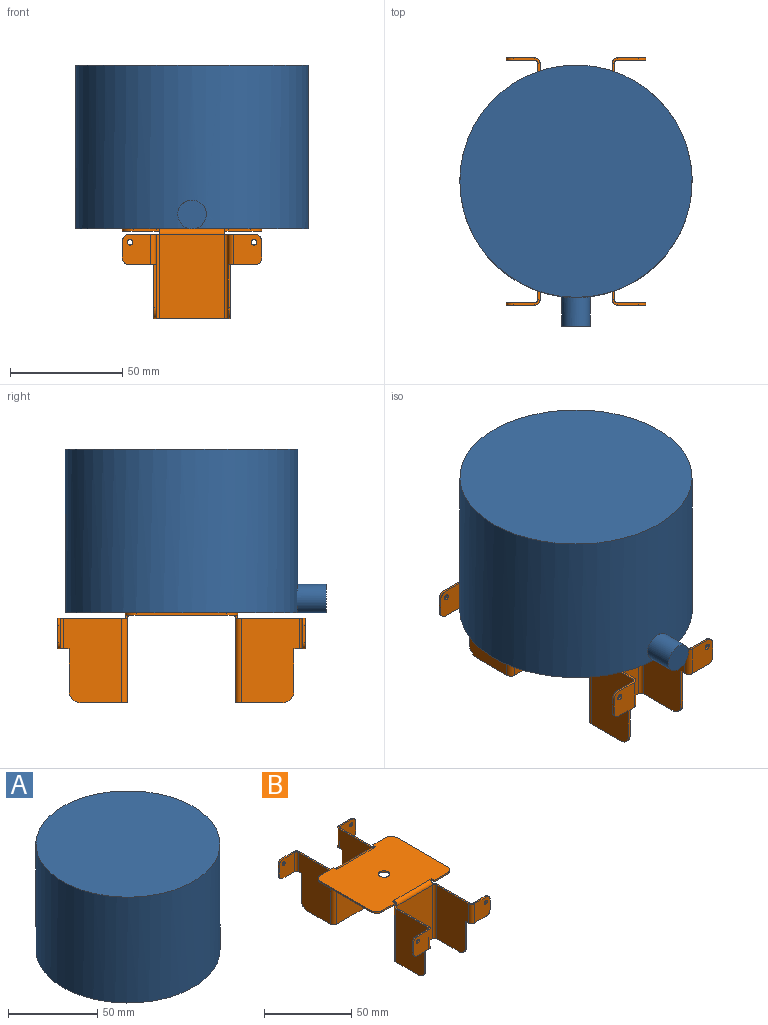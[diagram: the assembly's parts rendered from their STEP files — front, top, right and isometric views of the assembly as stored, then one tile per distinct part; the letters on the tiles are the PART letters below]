
ASSEMBLY  parts=2 mates=1
PART A: 5 faces, bbox 103.3x116x72.7 mm
  f0: cylinder r=51.65mm len=103.3mm, axis (0,0,-1), area 23466.2mm2, adj f1,f2,f4
  f1: plane 103.3x103.3mm, normal (0,0,1), area 8380.9mm2, adj f0
  f2: plane 103.3x103.3mm, normal (0,0,-1), area 8380.9mm2, adj f0
  f3: plane 12.7x12.7mm, normal (0,1,0), area 126.7mm2, adj f4
  f4: cylinder r=6.35mm len=13.09mm, axis (0,-1,0), area 514.5mm2, adj f0,f3
PART B: 127 faces, bbox 62x110x40 mm
  f0: plane 1.5x1mm, normal (0,-1,0), area 1.5mm2, adj f3,f15,f16,f123
  f1: plane 1.5x1mm, normal (0,1,0), area 1.5mm2, adj f5,f15,f16,f71
  f2: plane 2.5x1mm, normal (-1,0,0), area 2.5mm2, adj f10,f11,f15,f16
  f3: plane 2.5x1mm, normal (1,0,0), area 2.5mm2, adj f0,f9,f15,f16
  f4: plane 2.5x1mm, normal (1,0,0), area 2.5mm2, adj f6,f7,f15,f16
  f5: plane 2.5x1mm, normal (-1,0,0), area 2.5mm2, adj f1,f14,f15,f16
  f6: plane 1.5x1mm, normal (0,1,0), area 1.5mm2, adj f4,f15,f16,f70
  f7: plane 10x1mm, normal (0,1,0), area 10mm2, adj f4,f15,f16,f18
  f8: plane 40x1mm, normal (-1,0,0), area 40mm2, adj f15,f16,f18,f20
  f9: plane 10x1mm, normal (0,-1,0), area 10mm2, adj f3,f15,f16,f20
  f10: plane 1.5x1mm, normal (0,-1,0), area 1.5mm2, adj f2,f15,f16,f124
  f11: plane 10x1mm, normal (0,-1,0), area 10mm2, adj f2,f15,f16,f19
  f12: plane 40x1mm, normal (1,0,0), area 40mm2, adj f15,f16,f17,f19
  f13: cylinder r=3.26mm len=6.53mm, axis (0,0,1), area 20.5mm2, adj f15,f16
  f14: plane 10x1mm, normal (0,1,0), area 10mm2, adj f5,f15,f16,f17
  f15: plane 62x50mm, normal (0,0,1), area 2885.1mm2, adj f0,f1,f2,f3,f4,f5,f6,f7
  f16: plane 62x50mm, normal (0,0,-1), area 2885.1mm2, adj f0,f1,f2,f3,f4,f5,f6,f7
  f17: cylinder r=5mm len=5mm, axis (0,0,1), area 7.9mm2, adj f12,f14,f15,f16
  f18: cylinder r=5mm len=5mm, axis (0,0,1), area 7.9mm2, adj f7,f8,f15,f16
  f19: cylinder r=5mm len=5mm, axis (0,0,-1), area 7.9mm2, adj f11,f12,f15,f16
  f20: cylinder r=5mm len=5mm, axis (0,0,-1), area 7.9mm2, adj f8,f9,f15,f16
  f21: plane 29x1mm, normal (0,0,-1), area 29mm2, adj f22,f23,f44,f67
  f22: plane 37.5x29mm, normal (0,1,0), area 1087.5mm2, adj f21,f46,f69,f72
  f23: plane 37.5x29mm, normal (0,-1,0), area 1087.5mm2, adj f21,f45,f68,f73
  f24: plane 19x1mm, normal (0,1,0), area 19mm2, adj f25,f28,f29,f30
  f25: plane 2.5x1mm, normal (0,0,-1), area 2.5mm2, adj f24,f28,f29,f39
  f26: plane 26x1mm, normal (0,0,1), area 26mm2, adj f28,f29,f40,f43
  f27: plane 18.5x1mm, normal (0,0,-1), area 18.5mm2, adj f28,f29,f30,f44
  f28: plane 37.5x26mm, normal (1,0,0), area 909.6mm2, adj f24,f25,f26,f27,f30,f41,f46
  f29: plane 37.5x26mm, normal (-1,0,0), area 909.6mm2, adj f24,f25,f26,f27,f30,f42,f45
  f30: cylinder r=5mm len=5mm, axis (-1,0,0), area 7.9mm2, adj f24,f27,f28,f29
  f31: plane 7.5x1mm, normal (-1,0,0), area 7.5mm2, adj f35,f36,f37,f38
  f32: plane 9.5x1mm, normal (0,0,1), area 9.5mm2, adj f35,f36,f37,f40
  f33: cylinder r=1.25mm len=2.5mm, axis (0,1,0), area 7.9mm2, adj f35,f36
  f34: plane 9.5x1mm, normal (0,0,-1), area 9.5mm2, adj f35,f36,f38,f39
  f35: plane 13.5x12.5mm, normal (0,1,0), area 160mm2, adj f31,f32,f33,f34,f37,f38,f41
  f36: plane 13.5x12.5mm, normal (0,-1,0), area 160mm2, adj f31,f32,f33,f34,f37,f38,f42
  f37: cylinder r=3mm len=3mm, axis (0,1,0), area 4.7mm2, adj f31,f32,f35,f36
  f38: cylinder r=3mm len=3mm, axis (0,-1,0), area 4.7mm2, adj f31,f34,f35,f36
  f39: plane 2.5x2.5mm, normal (0,0,-1), area 3.1mm2, adj f25,f34,f41,f42
  f40: plane 2.5x2.5mm, normal (0,0,1), area 3.1mm2, adj f26,f32,f41,f42
  f41: cylinder r=2.5mm len=13.5mm, axis (0,0,-1), area 53mm2, adj f28,f35,f39,f40
  f42: cylinder r=1.5mm len=13.5mm, axis (0,0,-1), area 31.8mm2, adj f29,f36,f39,f40
  f43: plane 2.5x2.5mm, normal (0,0,1), area 3.1mm2, adj f26,f45,f46,f70
  f44: plane 2.5x2.5mm, normal (0,0,-1), area 3.1mm2, adj f21,f27,f45,f46
  f45: cylinder r=2.5mm len=37.5mm, axis (0,0,1), area 147.3mm2, adj f23,f29,f43,f44
  f46: cylinder r=1.5mm len=37.5mm, axis (0,0,1), area 88.4mm2, adj f22,f28,f43,f44
  f47: plane 2.5x1mm, normal (0,0,-1), area 2.5mm2, adj f48,f51,f52,f63
  f48: plane 19x1mm, normal (0,1,0), area 19mm2, adj f47,f51,f52,f53
  f49: plane 18.5x1mm, normal (0,0,-1), area 18.5mm2, adj f51,f52,f53,f67
  f50: plane 26x1mm, normal (0,0,1), area 26mm2, adj f51,f52,f62,f66
  f51: plane 37.5x26mm, normal (-1,0,0), area 909.6mm2, adj f47,f48,f49,f50,f53,f64,f69
  f52: plane 37.5x26mm, normal (1,0,0), area 909.6mm2, adj f47,f48,f49,f50,f53,f65,f68
  f53: cylinder r=5mm len=5mm, axis (1,0,0), area 7.9mm2, adj f48,f49,f51,f52
  f54: plane 7.5x1mm, normal (1,0,0), area 7.5mm2, adj f58,f59,f60,f61
  f55: plane 9.5x1mm, normal (0,0,-1), area 9.5mm2, adj f58,f59,f60,f63
  f56: cylinder r=1.25mm len=2.5mm, axis (0,1,0), area 7.9mm2, adj f58,f59
  f57: plane 9.5x1mm, normal (0,0,1), area 9.5mm2, adj f58,f59,f61,f62
  f58: plane 13.5x12.5mm, normal (0,1,0), area 160mm2, adj f54,f55,f56,f57,f60,f61,f64
  f59: plane 13.5x12.5mm, normal (0,-1,0), area 160mm2, adj f54,f55,f56,f57,f60,f61,f65
  f60: cylinder r=3mm len=3mm, axis (0,-1,0), area 4.7mm2, adj f54,f55,f58,f59
  f61: cylinder r=3mm len=3mm, axis (0,1,0), area 4.7mm2, adj f54,f57,f58,f59
  f62: plane 2.5x2.5mm, normal (0,0,1), area 3.1mm2, adj f50,f57,f64,f65
  f63: plane 2.5x2.5mm, normal (0,0,-1), area 3.1mm2, adj f47,f55,f64,f65
  f64: cylinder r=2.5mm len=13.5mm, axis (0,0,1), area 53mm2, adj f51,f58,f62,f63
  f65: cylinder r=1.5mm len=13.5mm, axis (0,0,1), area 31.8mm2, adj f52,f59,f62,f63
  f66: plane 2.5x2.5mm, normal (0,0,1), area 3.1mm2, adj f50,f68,f69,f71
  f67: plane 2.5x2.5mm, normal (0,0,-1), area 3.1mm2, adj f21,f49,f68,f69
  f68: cylinder r=2.5mm len=37.5mm, axis (0,0,1), area 147.3mm2, adj f23,f52,f66,f67
  f69: cylinder r=1.5mm len=37.5mm, axis (0,0,1), area 88.4mm2, adj f22,f51,f66,f67
  f70: plane 2.5x2.5mm, normal (-1,0,0), area 3.1mm2, adj f6,f43,f72,f73
  f71: plane 2.5x2.5mm, normal (1,0,0), area 3.1mm2, adj f1,f66,f72,f73
  f72: cylinder r=2.5mm len=29mm, axis (-1,0,0), area 113.9mm2, adj f15,f22,f70,f71
  f73: cylinder r=1.5mm len=29mm, axis (-1,0,0), area 68.3mm2, adj f16,f23,f70,f71
  f74: plane 29x1mm, normal (0,0,-1), area 29mm2, adj f75,f76,f97,f120
  f75: plane 37.5x29mm, normal (0,-1,0), area 1087.5mm2, adj f74,f99,f122,f125
  f76: plane 37.5x29mm, normal (0,1,0), area 1087.5mm2, adj f74,f98,f121,f126
  f77: plane 19x1mm, normal (0,-1,0), area 19mm2, adj f78,f81,f82,f83
  f78: plane 2.5x1mm, normal (0,0,-1), area 2.5mm2, adj f77,f81,f82,f92
  f79: plane 26x1mm, normal (0,0,1), area 26mm2, adj f81,f82,f93,f96
  f80: plane 18.5x1mm, normal (0,0,-1), area 18.5mm2, adj f81,f82,f83,f97
  f81: plane 37.5x26mm, normal (-1,0,0), area 909.6mm2, adj f77,f78,f79,f80,f83,f94,f99
  f82: plane 37.5x26mm, normal (1,0,0), area 909.6mm2, adj f77,f78,f79,f80,f83,f95,f98
  f83: cylinder r=5mm len=5mm, axis (1,0,0), area 7.9mm2, adj f77,f80,f81,f82
  f84: plane 7.5x1mm, normal (1,0,0), area 7.5mm2, adj f88,f89,f90,f91
  f85: plane 9.5x1mm, normal (0,0,1), area 9.5mm2, adj f88,f89,f90,f93
  f86: cylinder r=1.25mm len=2.5mm, axis (0,-1,0), area 7.9mm2, adj f88,f89
  f87: plane 9.5x1mm, normal (0,0,-1), area 9.5mm2, adj f88,f89,f91,f92
  f88: plane 13.5x12.5mm, normal (0,-1,0), area 160mm2, adj f84,f85,f86,f87,f90,f91,f94
  f89: plane 13.5x12.5mm, normal (0,1,0), area 160mm2, adj f84,f85,f86,f87,f90,f91,f95
  f90: cylinder r=3mm len=3mm, axis (0,-1,0), area 4.7mm2, adj f84,f85,f88,f89
  f91: cylinder r=3mm len=3mm, axis (0,1,0), area 4.7mm2, adj f84,f87,f88,f89
  f92: plane 2.5x2.5mm, normal (0,0,-1), area 3.1mm2, adj f78,f87,f94,f95
  f93: plane 2.5x2.5mm, normal (0,0,1), area 3.1mm2, adj f79,f85,f94,f95
  f94: cylinder r=2.5mm len=13.5mm, axis (0,0,-1), area 53mm2, adj f81,f88,f92,f93
  f95: cylinder r=1.5mm len=13.5mm, axis (0,0,-1), area 31.8mm2, adj f82,f89,f92,f93
  f96: plane 2.5x2.5mm, normal (0,0,1), area 3.1mm2, adj f79,f98,f99,f124
  f97: plane 2.5x2.5mm, normal (0,0,-1), area 3.1mm2, adj f74,f80,f98,f99
  f98: cylinder r=2.5mm len=37.5mm, axis (0,0,1), area 147.3mm2, adj f76,f82,f96,f97
  f99: cylinder r=1.5mm len=37.5mm, axis (0,0,1), area 88.4mm2, adj f75,f81,f96,f97
  f100: plane 2.5x1mm, normal (0,0,-1), area 2.5mm2, adj f101,f104,f105,f116
  f101: plane 19x1mm, normal (0,-1,0), area 19mm2, adj f100,f104,f105,f106
  f102: plane 18.5x1mm, normal (0,0,-1), area 18.5mm2, adj f104,f105,f106,f120
  f103: plane 26x1mm, normal (0,0,1), area 26mm2, adj f104,f105,f115,f119
  f104: plane 37.5x26mm, normal (1,0,0), area 909.6mm2, adj f100,f101,f102,f103,f106,f117,f122
  f105: plane 37.5x26mm, normal (-1,0,0), area 909.6mm2, adj f100,f101,f102,f103,f106,f118,f121
  f106: cylinder r=5mm len=5mm, axis (-1,0,0), area 7.9mm2, adj f101,f102,f104,f105
  f107: plane 7.5x1mm, normal (-1,0,0), area 7.5mm2, adj f111,f112,f113,f114
  f108: plane 9.5x1mm, normal (0,0,-1), area 9.5mm2, adj f111,f112,f113,f116
  f109: cylinder r=1.25mm len=2.5mm, axis (0,-1,0), area 7.9mm2, adj f111,f112
  f110: plane 9.5x1mm, normal (0,0,1), area 9.5mm2, adj f111,f112,f114,f115
  f111: plane 13.5x12.5mm, normal (0,-1,0), area 160mm2, adj f107,f108,f109,f110,f113,f114,f117
  f112: plane 13.5x12.5mm, normal (0,1,0), area 160mm2, adj f107,f108,f109,f110,f113,f114,f118
  f113: cylinder r=3mm len=3mm, axis (0,1,0), area 4.7mm2, adj f107,f108,f111,f112
  f114: cylinder r=3mm len=3mm, axis (0,-1,0), area 4.7mm2, adj f107,f110,f111,f112
  f115: plane 2.5x2.5mm, normal (0,0,1), area 3.1mm2, adj f103,f110,f117,f118
  f116: plane 2.5x2.5mm, normal (0,0,-1), area 3.1mm2, adj f100,f108,f117,f118
  f117: cylinder r=2.5mm len=13.5mm, axis (0,0,1), area 53mm2, adj f104,f111,f115,f116
  f118: cylinder r=1.5mm len=13.5mm, axis (0,0,1), area 31.8mm2, adj f105,f112,f115,f116
  f119: plane 2.5x2.5mm, normal (0,0,1), area 3.1mm2, adj f103,f121,f122,f123
  f120: plane 2.5x2.5mm, normal (0,0,-1), area 3.1mm2, adj f74,f102,f121,f122
  f121: cylinder r=2.5mm len=37.5mm, axis (0,0,1), area 147.3mm2, adj f76,f105,f119,f120
  f122: cylinder r=1.5mm len=37.5mm, axis (0,0,1), area 88.4mm2, adj f75,f104,f119,f120
  f123: plane 2.5x2.5mm, normal (-1,0,0), area 3.1mm2, adj f0,f119,f125,f126
  f124: plane 2.5x2.5mm, normal (1,0,0), area 3.1mm2, adj f10,f96,f125,f126
  f125: cylinder r=2.5mm len=29mm, axis (-1,0,0), area 113.9mm2, adj f15,f75,f123,f124
  f126: cylinder r=1.5mm len=29mm, axis (-1,0,0), area 68.3mm2, adj f16,f76,f123,f124
PLACE A rot(axis=(0,0,-1),180deg) t=(0,0,41)mm
PLACE B at identity fixed
MATE revolute A.f0 <-> B.f13  axis (0,0,-1) through (0,0,41)mm
